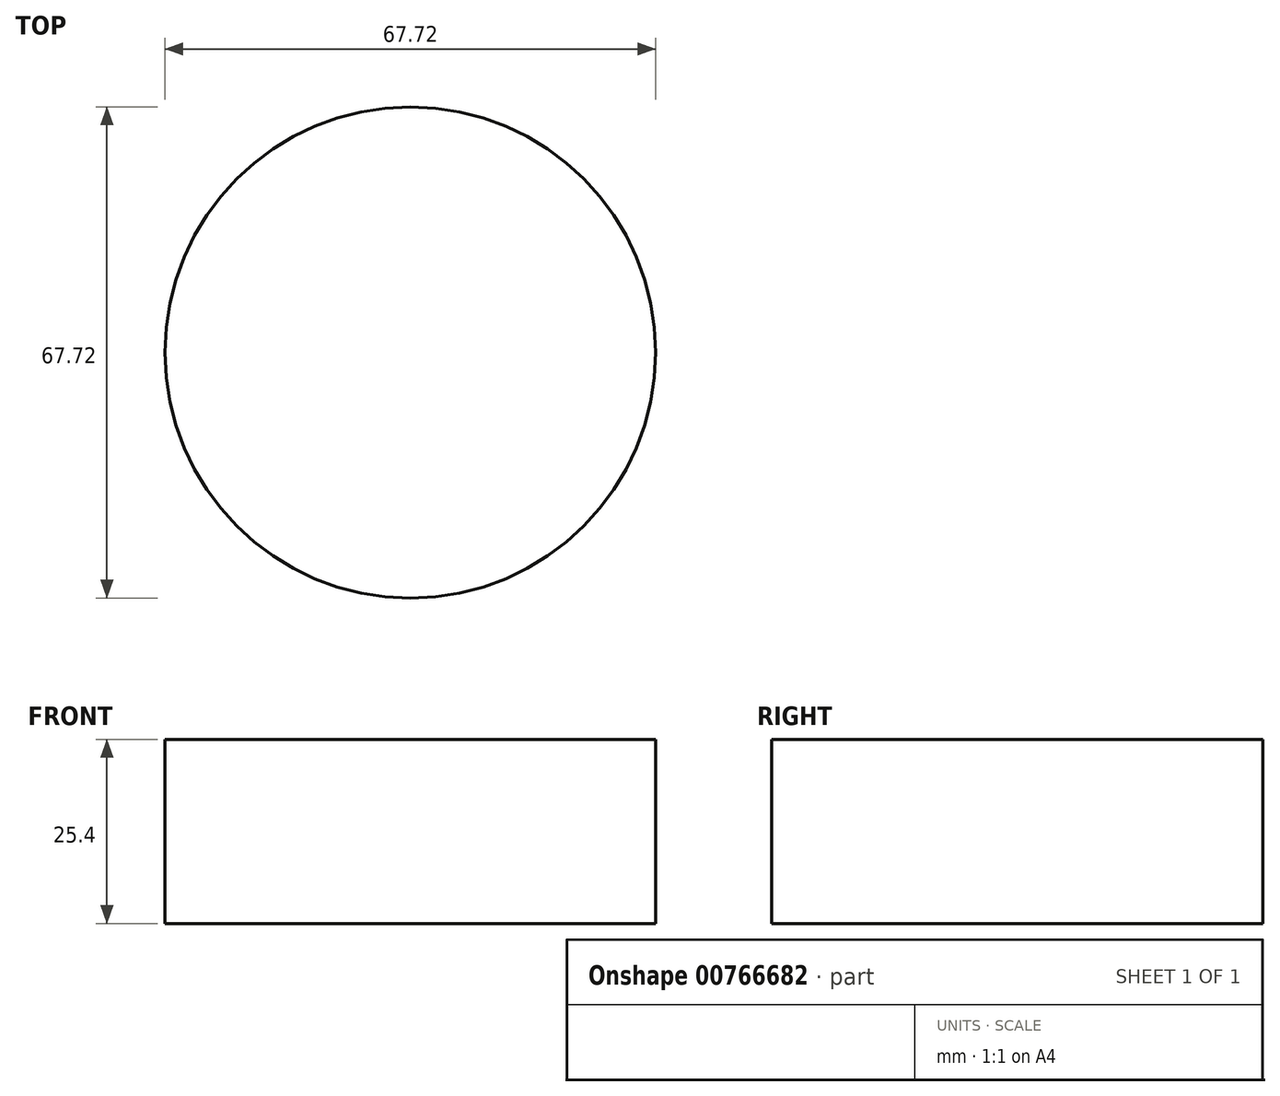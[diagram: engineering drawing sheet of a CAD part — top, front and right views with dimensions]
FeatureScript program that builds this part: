
annotation { "Feature Type Name" : "Feature", "Feature Type Description" : "" }
export const myFeature = defineFeature(function(context is Context, id is Id, definition is map)
    precondition{}
    {
        {
            var Q0;
            Q0=qCreatedBy(makeId("Top.planeOp"),FACE);
            var sketch = newSketch(context, id + "F0", { "sketchPlane" : qUnion([Q0])});
            skCircle(sketch, "E0", {"center": v(0, 0) * mm, "radius": 33.86 * mm});
            skSolve(sketch);
        }
        {
            var Q0;
            Q0=makeQuery(id+"F0.imprint","IMPRINT",FACE,{"disambiguationData":[TD([[makeQuery(id+"F0.imprint","IMPRINT",EDGE,{"derivedFrom":sQuery(id+"F0.wireOp",EDGE,"E0")}),1.0]])]});
            extrude(context, id + "F1", {"entities" : qUnion([Q0]), "depth" : 25.4 * mm, "offsetDistance" : 25.4 * mm});
        }
    });
